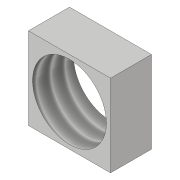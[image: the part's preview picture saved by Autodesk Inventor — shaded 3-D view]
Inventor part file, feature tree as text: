
AUTODESK INVENTOR PART (.ipt)
format: ipt  version: 2019 (Build 230136000, 136)  size: 98,304 bytes
history: native  units: in
note: dims shown in document units (in); Inventor stores cm internally (conversion verified against a paired STEP export)
features: extrude x2, sketch x2, thread x1
ambient origin geometry x8: Origin, YZ Plane, XZ Plane, XY Plane, X Axis, Y Axis, Z Axis, Center Point
bodies: Solid1 (feature_tree)
feature tree (5):
  extrude  "Extrusion1"  Depth=0.0787in
  extrude  "Extrusion2"  Depth=0.0394in
  thread  "Thread1"  [1 undecoded]
  sketch  "Sketch1"  dims[d0=0.0787in d1=0.0787in]
  sketch  "Sketch2"  dims[d2=0.0394in d3=0.0in d4=0.0394in d5=0.0394in d6=0.0394in d7=0.0394in d8=0.0709in d9=0.0in d10=0.0in d11=0.3937in d12=0.0in]
note: 1 required parameter value undecoded (feature->parameter linkage not recoverable at this tier; creation-order binding heuristic only, values carry confidence <= 0.55)
